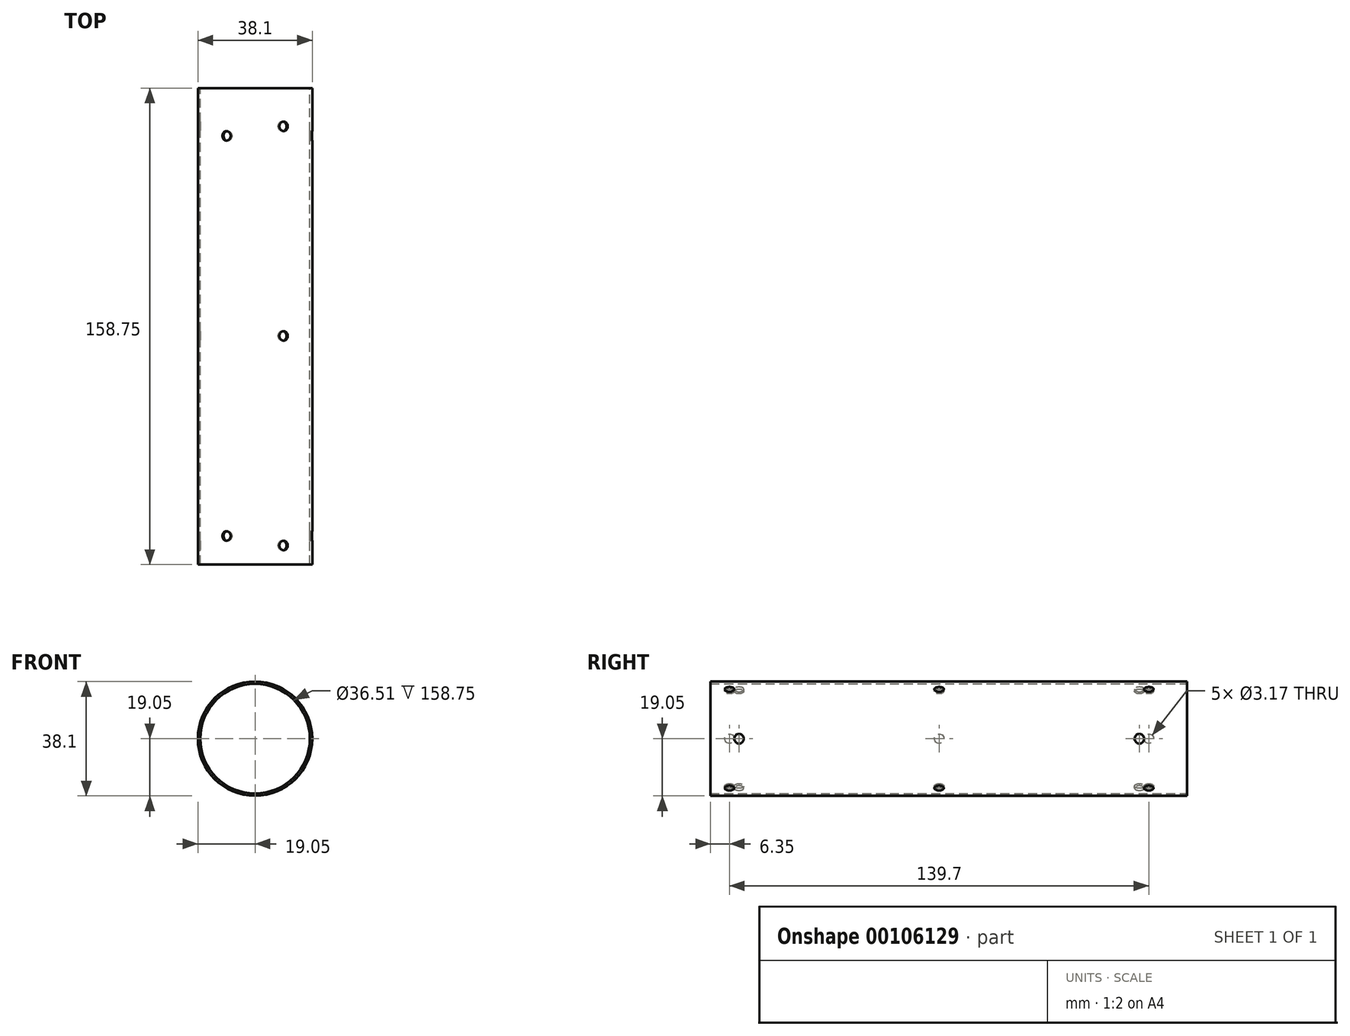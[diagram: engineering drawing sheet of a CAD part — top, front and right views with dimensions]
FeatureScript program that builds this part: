
annotation { "Feature Type Name" : "Feature", "Feature Type Description" : "" }
export const myFeature = defineFeature(function(context is Context, id is Id, definition is map)
    precondition{}
    {
        {
            var Q0;
            Q0=qCreatedBy(makeId("Right.planeOp"),FACE);
            var sketch = newSketch(context, id + "F0", { "sketchPlane" : qUnion([Q0])});
            skLineSegment(sketch, "E0", {"start": v(152.4, 0) * mm, "end": v(-152.4, 0) * mm, "construction": true});
            skLineSegment(sketch, "E1.bottom", {"start": v(-6.35, 19.05) * mm, "end": v(152.4, 19.05) * mm});
            skLineSegment(sketch, "E1.top", {"start": v(-6.35, 18.26) * mm, "end": v(152.4, 18.26) * mm});
            skLineSegment(sketch, "E1.left", {"start": v(-6.35, 19.05) * mm, "end": v(-6.35, 18.26) * mm});
            skLineSegment(sketch, "E1.right", {"start": v(152.4, 19.05) * mm, "end": v(152.4, 18.26) * mm});
            skSolve(sketch);
        }
        {
            var Q0;
            Q0 = qSketchRegion(id + "F0", true);
            var Q1;
            Q1=sQuery(id+"F0.wireOp",EDGE,"E0");
            revolve(context, id + "F1", {"entities" : qUnion([Q0]), "axis" : qUnion([Q1]), "revolveType" : RevolveType.FULL});
        }
        {
            var Q0;
            Q0=qCreatedBy(makeId("Front.planeOp"),FACE);
            var sketch = newSketch(context, id + "F2", { "sketchPlane" : qUnion([Q0])});
            skLineSegment(sketch, "E2", {"start": v(-19.05, 0) * mm, "end": v(19.05, 0) * mm, "construction": true});
            skLineSegment(sketch, "E3", {"start": v(0, 19.05) * mm, "end": v(0, -19.05) * mm, "construction": true});
            skLineSegment(sketch, "E4", {"start": v(-16.5, 9.53) * mm, "end": v(16.5, -9.53) * mm, "construction": true});
            skLineSegment(sketch, "E5.MirrorCS", {"start": v(16.5, 9.53) * mm, "end": v(-16.5, -9.53) * mm, "construction": true});
            skSolve(sketch);
        }
        {
            var Q0;
            Q0=sQuery(id+"F2.wireOp",VERTEX,"E5.MirrorCS.start");
            var Q1;
            Q1=sQuery(id+"F2.wireOp",VERTEX,"E5.MirrorCS.end");
            var Q2;
            Q2=sQuery(id+"F0.wireOp",VERTEX,"E0.start");
            cPlane(context, id + "F3", {"entities" : qUnion([Q0, Q1, Q2]), "cplaneType" : CPlaneType.THREE_POINT, "offset" : 25.4 * mm, "width" : 152.4 * mm, "height" : 152.4 * mm});
        }
        {
            var Q0;
            Q0=sQuery(id+"F2.wireOp",VERTEX,"E4.start");
            var Q1;
            Q1=sQuery(id+"F2.wireOp",VERTEX,"E4.end");
            var Q2;
            Q2=sQuery(id+"F0.wireOp",VERTEX,"E0.start");
            cPlane(context, id + "F4", {"entities" : qUnion([Q0, Q1, Q2]), "cplaneType" : CPlaneType.THREE_POINT, "offset" : 25.4 * mm, "width" : 152.4 * mm, "height" : 152.4 * mm});
        }
        {
            var Q0;
            Q0=qCreatedBy(makeId("Right.planeOp"),FACE);
            var sketch = newSketch(context, id + "F5", { "sketchPlane" : qUnion([Q0])});
            skCircle(sketch, "E6", {"center": v(3.18, 0) * mm, "radius": 1.59 * mm});
            skCircle(sketch, "E7", {"center": v(136.53, 0) * mm, "radius": 1.59 * mm});
            skSolve(sketch);
        }
        {
            var Q0;
            Q0 = qSketchRegion(id + "F5", true);
            var Q1;
            Q1=makeQuery(id+"F1.opRevolve","SWEPT_FACE",FACE,{"disambiguationData":[OSD([sQuery(id+"F0.wireOp",EDGE,"E1.bottom")])]});
            extrude(context, id + "F6", {"entities" : qUnion([Q0]), "operationType" : NewBodyOperationType.REMOVE, "endBound" : BoundingType.UP_TO_SURFACE, "endBoundEntityFace" : qUnion([Q1]), "depth" : 25.4 * mm});
        }
        {
            var Q0;
            Q0=qCreatedBy(makeId("Right.planeOp"),FACE);
            var sketch = newSketch(context, id + "F7", { "sketchPlane" : qUnion([Q0])});
            skCircle(sketch, "E8", {"center": v(0, 0) * mm, "radius": 1.59 * mm});
            skCircle(sketch, "E9", {"center": v(69.85, 0) * mm, "radius": 1.59 * mm});
            skCircle(sketch, "E10", {"center": v(139.7, 0) * mm, "radius": 1.59 * mm});
            skSolve(sketch);
        }
        {
            var Q0;
            Q0 = qSketchRegion(id + "F7", true);
            var Q1;
            Q1=makeQuery(id+"F1.opRevolve","SWEPT_FACE",FACE,{"disambiguationData":[OSD([sQuery(id+"F0.wireOp",EDGE,"E1.bottom")])]});
            extrude(context, id + "F8", {"entities" : qUnion([Q0]), "operationType" : NewBodyOperationType.REMOVE, "endBound" : BoundingType.UP_TO_SURFACE, "oppositeDirection" : true, "endBoundEntityFace" : qUnion([Q1]), "depth" : 25.4 * mm});
        }
        {
            var Q0;
            Q0=qCreatedBy(id+"F3.planeOp",FACE);
            var sketch = newSketch(context, id + "F9", { "sketchPlane" : qUnion([Q0])});
            skCircle(sketch, "E11", {"center": v(0, 3.17) * mm, "radius": 1.59 * mm});
            skCircle(sketch, "E12", {"center": v(0, 136.53) * mm, "radius": 1.59 * mm});
            skSolve(sketch);
        }
        {
            var Q0;
            Q0 = qSketchRegion(id + "F9", true);
            var Q1;
            Q1=makeQuery(id+"F1.opRevolve","SWEPT_FACE",FACE,{"disambiguationData":[OSD([sQuery(id+"F0.wireOp",EDGE,"E1.bottom")])]});
            extrude(context, id + "F10", {"entities" : qUnion([Q0]), "operationType" : NewBodyOperationType.REMOVE, "endBound" : BoundingType.UP_TO_SURFACE, "endBoundEntityFace" : qUnion([Q1]), "depth" : 25.4 * mm});
        }
        {
            var Q0;
            Q0=qCreatedBy(id+"F3.planeOp",FACE);
            var sketch = newSketch(context, id + "F11", { "sketchPlane" : qUnion([Q0])});
            skCircle(sketch, "E13", {"center": v(0, 0) * mm, "radius": 1.59 * mm});
            skCircle(sketch, "E14", {"center": v(0, 69.85) * mm, "radius": 1.59 * mm});
            skCircle(sketch, "E15", {"center": v(0, 139.7) * mm, "radius": 1.59 * mm});
            skSolve(sketch);
        }
        {
            var Q0;
            Q0 = qSketchRegion(id + "F11", true);
            var Q1;
            Q1=makeQuery(id+"F1.opRevolve","SWEPT_FACE",FACE,{"disambiguationData":[OSD([sQuery(id+"F0.wireOp",EDGE,"E1.bottom")])]});
            extrude(context, id + "F12", {"entities" : qUnion([Q0]), "operationType" : NewBodyOperationType.REMOVE, "endBound" : BoundingType.UP_TO_SURFACE, "oppositeDirection" : true, "endBoundEntityFace" : qUnion([Q1]), "depth" : 25.4 * mm});
        }
        {
            var Q0;
            Q0=qCreatedBy(id+"F4.planeOp",FACE);
            var sketch = newSketch(context, id + "F13", { "sketchPlane" : qUnion([Q0])});
            skCircle(sketch, "E16", {"center": v(0, -3.18) * mm, "radius": 1.59 * mm});
            skCircle(sketch, "E17", {"center": v(0, -136.53) * mm, "radius": 1.59 * mm});
            skSolve(sketch);
        }
        {
            var Q0;
            Q0 = qSketchRegion(id + "F13", true);
            var Q1;
            Q1=makeQuery(id+"F1.opRevolve","SWEPT_FACE",FACE,{"disambiguationData":[OSD([sQuery(id+"F0.wireOp",EDGE,"E1.bottom")])]});
            extrude(context, id + "F14", {"entities" : qUnion([Q0]), "operationType" : NewBodyOperationType.REMOVE, "endBound" : BoundingType.UP_TO_SURFACE, "endBoundEntityFace" : qUnion([Q1]), "depth" : 25.4 * mm});
        }
        {
            var Q0;
            Q0=qCreatedBy(id+"F4.planeOp",FACE);
            var sketch = newSketch(context, id + "F15", { "sketchPlane" : qUnion([Q0])});
            skCircle(sketch, "E18", {"center": v(0, 0) * mm, "radius": 1.59 * mm});
            skCircle(sketch, "E19", {"center": v(0, -69.85) * mm, "radius": 1.59 * mm});
            skCircle(sketch, "E20", {"center": v(0, -139.7) * mm, "radius": 1.59 * mm});
            skSolve(sketch);
        }
        {
            var Q0;
            Q0 = qSketchRegion(id + "F15", true);
            var Q1;
            Q1=makeQuery(id+"F1.opRevolve","SWEPT_FACE",FACE,{"disambiguationData":[OSD([sQuery(id+"F0.wireOp",EDGE,"E1.bottom")])]});
            extrude(context, id + "F16", {"entities" : qUnion([Q0]), "operationType" : NewBodyOperationType.REMOVE, "endBound" : BoundingType.UP_TO_SURFACE, "oppositeDirection" : true, "endBoundEntityFace" : qUnion([Q1]), "depth" : 25.4 * mm});
        }
    });
